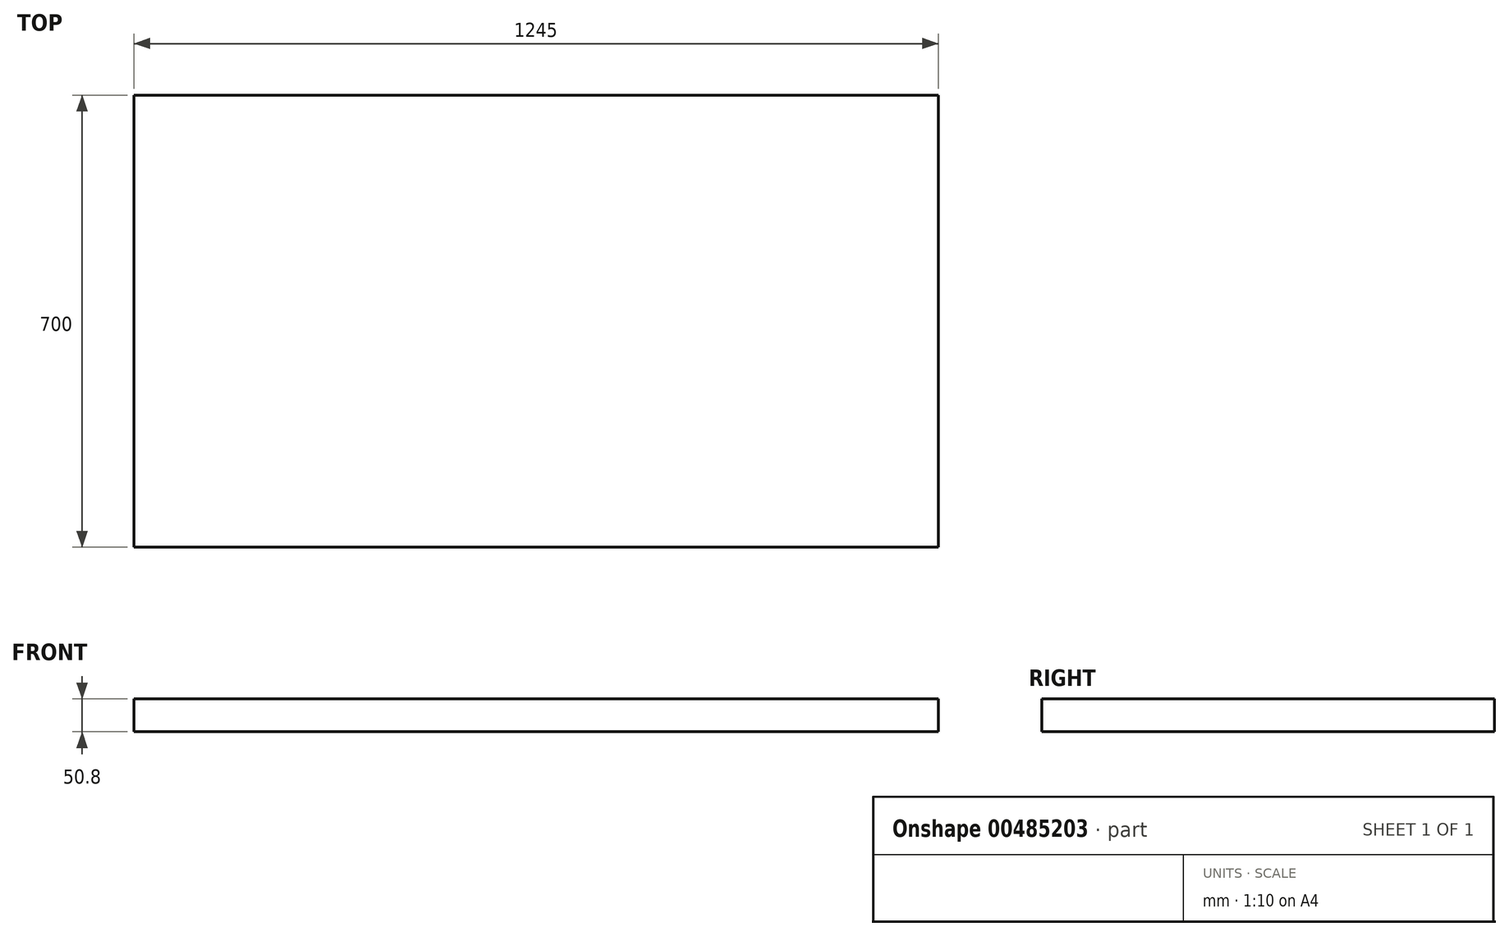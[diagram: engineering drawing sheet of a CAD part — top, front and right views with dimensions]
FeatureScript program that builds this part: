
annotation { "Feature Type Name" : "Feature", "Feature Type Description" : "" }
export const myFeature = defineFeature(function(context is Context, id is Id, definition is map)
    precondition{}
    {
        {
            var Q0;
            Q0=qCreatedBy(makeId("Top.planeOp"),FACE);
            var sketch = newSketch(context, id + "F0", { "sketchPlane" : qUnion([Q0])});
            skLineSegment(sketch, "E0.bottom", {"start": v(622.5, 350) * mm, "end": v(-622.5, 350) * mm});
            skLineSegment(sketch, "E0.top", {"start": v(622.5, -350) * mm, "end": v(-622.5, -350) * mm});
            skLineSegment(sketch, "E0.left", {"start": v(622.5, 350) * mm, "end": v(622.5, -350) * mm});
            skLineSegment(sketch, "E0.right", {"start": v(-622.5, 350) * mm, "end": v(-622.5, -350) * mm});
            skPoint(sketch, "E0.middle", {"position": v(0, 0) * mm});
            skSolve(sketch);
        }
        {
            var Q0;
            Q0=makeQuery(id+"F0.imprint","IMPRINT",FACE,{"disambiguationData":[TD([[makeQuery(id+"F0.imprint","IMPRINT",EDGE,{"derivedFrom":sQuery(id+"F0.wireOp",EDGE,"E0.bottom")}),1.0]])]});
            extrude(context, id + "F1", {"entities" : qUnion([Q0]), "depth" : 50.8 * mm});
        }
    });
